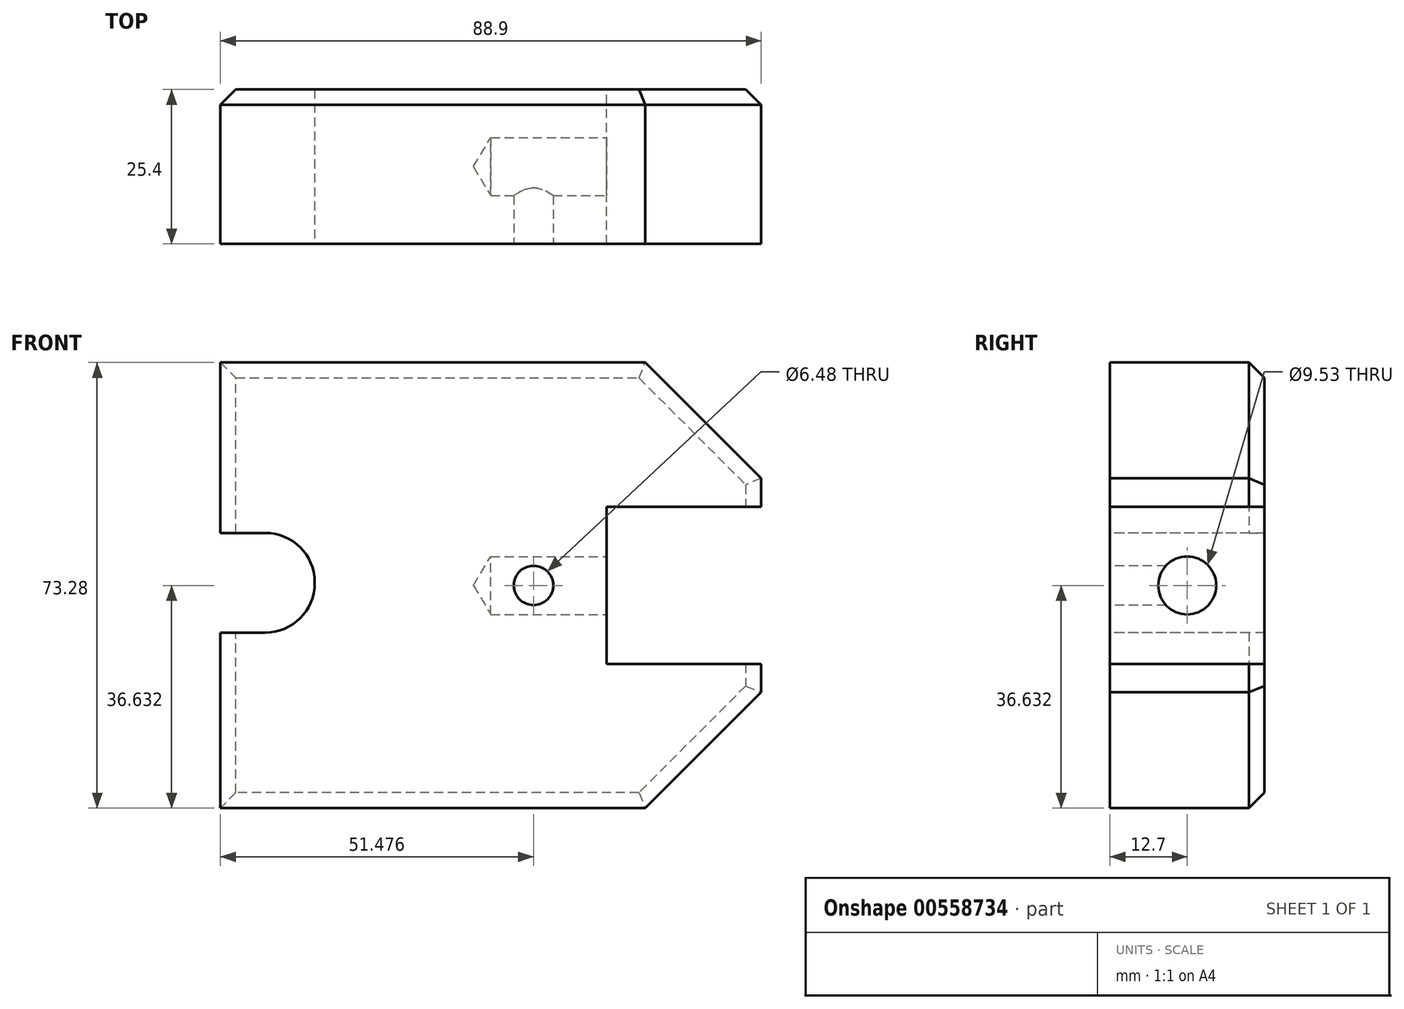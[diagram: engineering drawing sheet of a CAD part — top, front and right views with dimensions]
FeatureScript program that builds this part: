
annotation { "Feature Type Name" : "Feature", "Feature Type Description" : "" }
export const myFeature = defineFeature(function(context is Context, id is Id, definition is map)
    precondition{}
    {
        {
            var Q0;
            Q0=qCreatedBy(makeId("Front.planeOp"),FACE);
            var sketch = newSketch(context, id + "F0", { "sketchPlane" : qUnion([Q0])});
            skLineSegment(sketch, "E0", {"start": v(0, 0) * mm, "end": v(-88.9, 0) * mm});
            skLineSegment(sketch, "E1", {"start": v(-88.9, 0) * mm, "end": v(-88.9, 73.28) * mm});
            skLineSegment(sketch, "E2", {"start": v(-88.9, 73.28) * mm, "end": v(0, 73.28) * mm});
            skLineSegment(sketch, "E3", {"start": v(0, 73.28) * mm, "end": v(0, 49.53) * mm});
            skLineSegment(sketch, "E4", {"start": v(0, 0) * mm, "end": v(0, 23.73) * mm});
            skLineSegment(sketch, "E5", {"start": v(0, 49.53) * mm, "end": v(-25.4, 49.53) * mm});
            skLineSegment(sketch, "E6", {"start": v(-25.4, 49.53) * mm, "end": v(-25.4, 23.73) * mm});
            skLineSegment(sketch, "E7", {"start": v(-25.4, 23.73) * mm, "end": v(0, 23.73) * mm});
            skSolve(sketch);
        }
        {
            var Q0;
            Q0=makeQuery(id+"F0.imprint","IMPRINT",FACE,{"disambiguationData":[TD([[makeQuery(id+"F0.imprint","IMPRINT",EDGE,{"derivedFrom":sQuery(id+"F0.wireOp",EDGE,"E0")}),-1.0]])]});
            extrude(context, id + "F1", {"entities" : qUnion([Q0]), "depth" : 25.4 * mm, "offsetDistance" : 25.4 * mm});
        }
        {
            var Q0;
            Q0=makeQuery(id+"F1.opExtrude","CAP_EDGE",EDGE,{"disambiguationData":[OSD([sQuery(id+"F0.wireOp",EDGE,"E2")])],"isStart":true});
            var Q1;
            Q1=makeQuery(id+"F1.opExtrude","CAP_EDGE",EDGE,{"disambiguationData":[OSD([sQuery(id+"F0.wireOp",EDGE,"E3")])],"isStart":true});
            var Q2;
            Q2=makeQuery(id+"F1.opExtrude","CAP_EDGE",EDGE,{"disambiguationData":[OSD([sQuery(id+"F0.wireOp",EDGE,"E1")])],"isStart":true});
            var Q3;
            Q3=makeQuery(id+"F1.opExtrude","CAP_EDGE",EDGE,{"disambiguationData":[OSD([sQuery(id+"F0.wireOp",EDGE,"E0")])],"isStart":true});
            var Q4;
            Q4=makeQuery(id+"F1.opExtrude","CAP_EDGE",EDGE,{"disambiguationData":[OSD([sQuery(id+"F0.wireOp",EDGE,"E4")])],"isStart":true});
            chamfer(context, id + "F2", {"entities" : qUnion([Q0, Q1, Q2, Q3, Q4]), "width" : 2.54 * mm, "tangentPropagation" : true});
        }
        {
            var Q0;
            Q0=makeQuery(id+"F1.opExtrude","SWEPT_EDGE",EDGE,{"disambiguationData":[OSD([sQuery(id+"F0.wireOp",EDGE,"E2"),sQuery(id+"F0.wireOp",EDGE,"E3")])]});
            var Q1;
            Q1=makeQuery(id+"F1.opExtrude","SWEPT_EDGE",EDGE,{"disambiguationData":[OSD([sQuery(id+"F0.wireOp",EDGE,"E0"),sQuery(id+"F0.wireOp",EDGE,"E4")])]});
            chamfer(context, id + "F3", {"entities" : qUnion([Q0, Q1]), "width" : 19.05 * mm, "tangentPropagation" : true});
        }
        {
            var Q0;
            {var subQ0=sQuery(id+"F0.wireOp",EDGE,"E3");var subQ1=sQuery(id+"F0.wireOp",EDGE,"E2");Q0=makeQuery(id+"F3.opChamfer","BLEND_EDGE",EDGE,{"blendedFrom":[makeQuery(id+"F1.opExtrude","SWEPT_EDGE",EDGE,{"disambiguationData":[OSD([subQ1,subQ0])]}),makeQuery(id+"F1.opExtrude","CAP_FACE",FACE,{"disambiguationData":[OSD([sQuery(id+"F0.wireOp",EDGE,"E0"),sQuery(id+"F0.wireOp",EDGE,"E1"),subQ1,subQ0,sQuery(id+"F0.wireOp",EDGE,"E4"),sQuery(id+"F0.wireOp",EDGE,"E5"),sQuery(id+"F0.wireOp",EDGE,"E6"),sQuery(id+"F0.wireOp",EDGE,"E7")])],"isStart":true})],"blendedInto":[makeQuery(id+"F1.opExtrude","CAP_FACE",FACE,{"disambiguationData":[OSD([sQuery(id+"F0.wireOp",EDGE,"E0"),sQuery(id+"F0.wireOp",EDGE,"E1"),subQ1,subQ0,sQuery(id+"F0.wireOp",EDGE,"E4"),sQuery(id+"F0.wireOp",EDGE,"E5"),sQuery(id+"F0.wireOp",EDGE,"E6"),sQuery(id+"F0.wireOp",EDGE,"E7")])],"isStart":true})]});}
            var Q1;
            {var subQ0=sQuery(id+"F0.wireOp",EDGE,"E4");var subQ1=sQuery(id+"F0.wireOp",EDGE,"E0");Q1=makeQuery(id+"F3.opChamfer","BLEND_EDGE",EDGE,{"blendedFrom":[makeQuery(id+"F1.opExtrude","SWEPT_EDGE",EDGE,{"disambiguationData":[OSD([subQ1,subQ0])]}),makeQuery(id+"F1.opExtrude","CAP_FACE",FACE,{"disambiguationData":[OSD([subQ1,sQuery(id+"F0.wireOp",EDGE,"E1"),sQuery(id+"F0.wireOp",EDGE,"E2"),sQuery(id+"F0.wireOp",EDGE,"E3"),subQ0,sQuery(id+"F0.wireOp",EDGE,"E5"),sQuery(id+"F0.wireOp",EDGE,"E6"),sQuery(id+"F0.wireOp",EDGE,"E7")])],"isStart":true})],"blendedInto":[makeQuery(id+"F1.opExtrude","CAP_FACE",FACE,{"disambiguationData":[OSD([subQ1,sQuery(id+"F0.wireOp",EDGE,"E1"),sQuery(id+"F0.wireOp",EDGE,"E2"),sQuery(id+"F0.wireOp",EDGE,"E3"),subQ0,sQuery(id+"F0.wireOp",EDGE,"E5"),sQuery(id+"F0.wireOp",EDGE,"E6"),sQuery(id+"F0.wireOp",EDGE,"E7")])],"isStart":true})]});}
            chamfer(context, id + "F4", {"entities" : qUnion([Q0, Q1]), "width" : 2.54 * mm, "tangentPropagation" : true});
        }
        {
            var Q0;
            Q0=makeQuery(id+"F1.opExtrude","CAP_FACE",FACE,{"disambiguationData":[OSD([sQuery(id+"F0.wireOp",EDGE,"E0"),sQuery(id+"F0.wireOp",EDGE,"E1"),sQuery(id+"F0.wireOp",EDGE,"E2"),sQuery(id+"F0.wireOp",EDGE,"E3"),sQuery(id+"F0.wireOp",EDGE,"E4"),sQuery(id+"F0.wireOp",EDGE,"E5"),sQuery(id+"F0.wireOp",EDGE,"E6"),sQuery(id+"F0.wireOp",EDGE,"E7")])],"isStart":false});
            var sketch = newSketch(context, id + "F5", { "sketchPlane" : qUnion([Q0])});
            skLineSegment(sketch, "E8", {"start": v(-88.9, 45.27) * mm, "end": v(-88.9, 28.87) * mm});
            skLineSegment(sketch, "E9", {"start": v(-88.9, 28.87) * mm, "end": v(-73.4, 28.87) * mm});
            skLineSegment(sketch, "E10", {"start": v(-73.4, 28.87) * mm, "end": v(-73.4, 45.27) * mm});
            skLineSegment(sketch, "E11", {"start": v(-73.4, 45.27) * mm, "end": v(-88.9, 45.27) * mm});
            skSolve(sketch);
        }
        {
            var Q0;
            Q0=makeQuery(id+"F5.imprint","IMPRINT",FACE,{"disambiguationData":[TD([[makeQuery(id+"F5.imprint","IMPRINT",EDGE,{"derivedFrom":sQuery(id+"F5.wireOp",EDGE,"E8")}),-1.0]])]});
            extrude(context, id + "F6", {"entities" : qUnion([Q0]), "operationType" : NewBodyOperationType.REMOVE, "oppositeDirection" : true, "depth" : 25.4 * mm, "offsetDistance" : 25.4 * mm});
        }
        {
            var Q0;
            Q0=makeQuery(id+"F6.boolean.opBoolean","COPY",EDGE,{"derivedFrom":makeQuery(id+"F6.opExtrude","SWEPT_EDGE",EDGE,{"disambiguationData":[OSD([sQuery(id+"F5.wireOp",EDGE,"E10"),sQuery(id+"F5.wireOp",EDGE,"E11")])]})});
            var Q1;
            Q1=makeQuery(id+"F6.boolean.opBoolean","COPY",EDGE,{"derivedFrom":makeQuery(id+"F6.opExtrude","SWEPT_EDGE",EDGE,{"disambiguationData":[OSD([sQuery(id+"F5.wireOp",EDGE,"E9"),sQuery(id+"F5.wireOp",EDGE,"E10")])]})});
            fillet(context, id + "F7", {"entities" : qUnion([Q0, Q1]), "radius" : 8.13 * mm, "tangentPropagation" : true, "allowEdgeOverflow" : false});
        }
        {
            var Q0;
            Q0=makeQuery(id+"F1.opExtrude","SWEPT_FACE",FACE,{"disambiguationData":[OSD([sQuery(id+"F0.wireOp",EDGE,"E6")])]});
            var sketch = newSketch(context, id + "F8", { "sketchPlane" : qUnion([Q0])});
            skPoint(sketch, "E12", {"position": v(-12.7, 36.63) * mm});
            skPoint(sketch, "E12.positionSnap0", {"position": v(-12.7, 49.53) * mm});
            skPoint(sketch, "E12.positionSnap1", {"position": v(0, 36.63) * mm});
            skSolve(sketch);
        }
        {
            var Q0;
            Q0=sQuery(id+"F8.wireOp",VERTEX,"E12");
            var Q1;
            Q1=makeQuery(id+"F1.opExtrude","SWEPT_BODY",BODY,{"disambiguationData":[OSD([sQuery(id+"F0.wireOp",EDGE,"E0"),sQuery(id+"F0.wireOp",EDGE,"E1"),sQuery(id+"F0.wireOp",EDGE,"E2"),sQuery(id+"F0.wireOp",EDGE,"E3"),sQuery(id+"F0.wireOp",EDGE,"E4"),sQuery(id+"F0.wireOp",EDGE,"E5"),sQuery(id+"F0.wireOp",EDGE,"E6"),sQuery(id+"F0.wireOp",EDGE,"E7")])]});
            hole(context, id + "F9", {"style" : HoleStyle.SIMPLE, "endStyle" : HoleEndStyle.BLIND, "holeDiameter" : 9.52 * mm, "holeDepth" : 19.05 * mm, "isTappedThrough" : true, "tappedDepth" : 12.7 * mm, "tapClearance" : 3, "locations" : qUnion([Q0]), "scope" : qUnion([Q1])});
        }
        {
            var Q0;
            Q0=makeQuery(id+"F1.opExtrude","CAP_FACE",FACE,{"disambiguationData":[OSD([sQuery(id+"F0.wireOp",EDGE,"E0"),sQuery(id+"F0.wireOp",EDGE,"E1"),sQuery(id+"F0.wireOp",EDGE,"E2"),sQuery(id+"F0.wireOp",EDGE,"E3"),sQuery(id+"F0.wireOp",EDGE,"E4"),sQuery(id+"F0.wireOp",EDGE,"E5"),sQuery(id+"F0.wireOp",EDGE,"E6"),sQuery(id+"F0.wireOp",EDGE,"E7")])],"isStart":false});
            var sketch = newSketch(context, id + "F10", { "sketchPlane" : qUnion([Q0])});
            skPoint(sketch, "E13", {"position": v(-37.42, 36.63) * mm});
            skPoint(sketch, "E13.positionSnap0", {"position": v(-25.4, 36.63) * mm});
            skSolve(sketch);
        }
        {
            var Q0;
            Q0=sQuery(id+"F10.wireOp",VERTEX,"E13");
            var Q1;
            Q1=makeQuery(id+"F1.opExtrude","SWEPT_BODY",BODY,{"disambiguationData":[OSD([sQuery(id+"F0.wireOp",EDGE,"E0"),sQuery(id+"F0.wireOp",EDGE,"E1"),sQuery(id+"F0.wireOp",EDGE,"E2"),sQuery(id+"F0.wireOp",EDGE,"E3"),sQuery(id+"F0.wireOp",EDGE,"E4"),sQuery(id+"F0.wireOp",EDGE,"E5"),sQuery(id+"F0.wireOp",EDGE,"E6"),sQuery(id+"F0.wireOp",EDGE,"E7")])]});
            hole(context, id + "F11", {"style" : HoleStyle.SIMPLE, "endStyle" : HoleEndStyle.BLIND, "holeDiameter" : 6.48 * mm, "holeDepth" : 14.27 * mm, "isTappedThrough" : true, "tappedDepth" : 12.7 * mm, "tapClearance" : 3, "locations" : qUnion([Q0]), "scope" : qUnion([Q1])});
        }
    });
